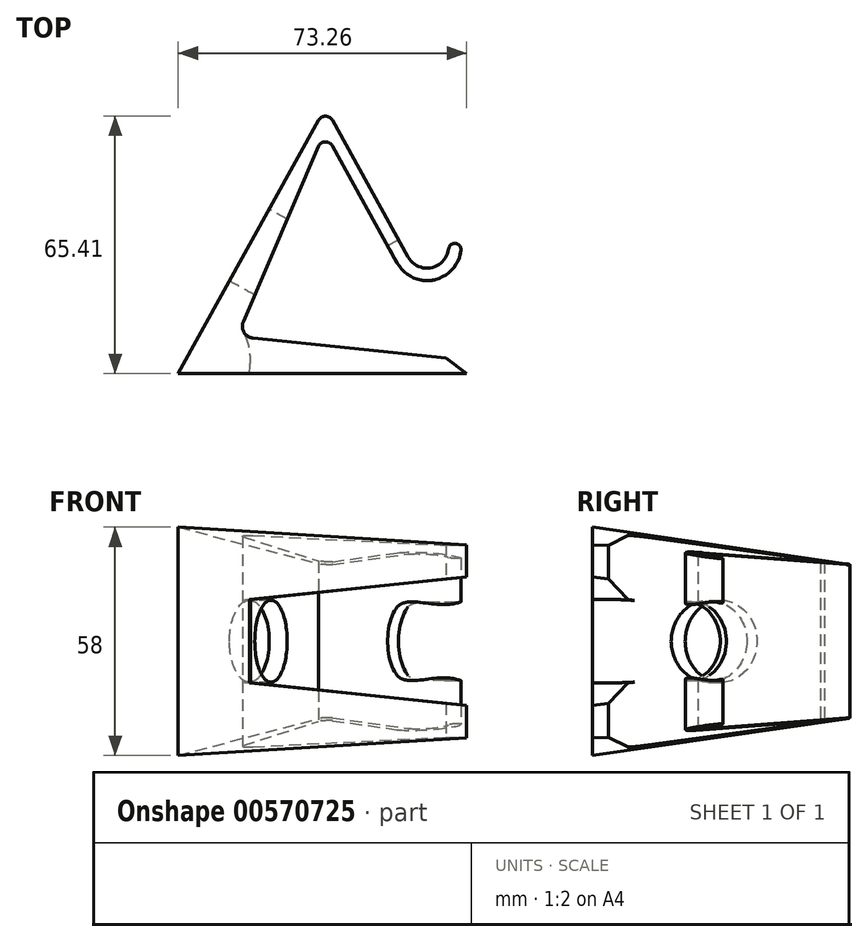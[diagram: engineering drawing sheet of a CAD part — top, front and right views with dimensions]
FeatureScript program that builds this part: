
annotation { "Feature Type Name" : "Feature", "Feature Type Description" : "" }
export const myFeature = defineFeature(function(context is Context, id is Id, definition is map)
    precondition{}
    {
        {
            var Q0;
            Q0=qCreatedBy(makeId("Top.planeOp"),FACE);
            var sketch = newSketch(context, id + "F0", { "sketchPlane" : qUnion([Q0])});
            skLineSegment(sketch, "E0", {"start": v(10.38, 11.62) * mm, "end": v(27.88, 11.62) * mm, "construction": true});
            skLineSegment(sketch, "E1", {"start": v(7.89, 47.93) * mm, "end": v(-27.76, -16.45) * mm});
            skPoint(sketch, "E2.visualSharp", {"position": v(9.6, 51.03) * mm});
            skArc(sketch, "E2.filletArc", {"start": v(11.39, 47.93) * mm, "mid": v(9.64, 48.96) * mm, "end": v(7.89, 47.93) * mm});
            skPoint(sketch, "E3.visualSharp", {"position": v(-23.5, -14.09) * mm});
            skLineSegment(sketch, "E4", {"start": v(11.39, 47.93) * mm, "end": v(30.65, 13.15) * mm});
            skLineSegment(sketch, "E5", {"start": v(-11.22, -3.27) * mm, "end": v(7.89, 41.4) * mm});
            skArc(sketch, "E6", {"start": v(11.39, 41.4) * mm, "mid": v(9.64, 42.44) * mm, "end": v(7.89, 41.4) * mm});
            skLineSegment(sketch, "E7", {"start": v(11.39, 41.4) * mm, "end": v(27.88, 11.62) * mm});
            skArc(sketch, "E8", {"start": v(30.65, 13.15) * mm, "mid": v(36.56, 10.43) * mm, "end": v(40.93, 15.25) * mm});
            skLineSegment(sketch, "E9", {"start": v(30.65, 13.15) * mm, "end": v(48.91, 23.27) * mm, "construction": true});
            skArc(sketch, "E10", {"start": v(27.88, 11.62) * mm, "mid": v(37.19, 7.33) * mm, "end": v(44.07, 14.92) * mm});
            skPoint(sketch, "E11.orphan", {"position": v(28.74, 11.62) * mm});
            skArc(sketch, "E12", {"start": v(44.07, 14.92) * mm, "mid": v(42.66, 16.66) * mm, "end": v(40.93, 15.25) * mm});
            skPoint(sketch, "E12.first.point", {"position": v(40.93, 15.25) * mm});
            skPoint(sketch, "E12.second.point", {"position": v(44.07, 14.92) * mm});
            skPoint(sketch, "E12.third.point", {"position": v(43.23, 16.49) * mm});
            skLineSegment(sketch, "E13", {"start": v(-27.76, -16.45) * mm, "end": v(45.5, -16.45) * mm});
            skLineSegment(sketch, "E14", {"start": v(-7.91, -7.53) * mm, "end": v(34.87, -11.9) * mm});
            skLineSegment(sketch, "E15", {"start": v(-7.91, -7.53) * mm, "end": v(-8.77, -7.44) * mm});
            skPoint(sketch, "E16.visualSharp", {"position": v(-12.83, -7.02) * mm});
            skArc(sketch, "E16.filletArc", {"start": v(-11.22, -3.27) * mm, "mid": v(-11.05, -5.98) * mm, "end": v(-8.77, -7.44) * mm});
            skLineSegment(sketch, "E17", {"start": v(34.87, -11.9) * mm, "end": v(40.25, -12.45) * mm});
            skLineSegment(sketch, "E18", {"start": v(40.25, -12.45) * mm, "end": v(45.5, -16.45) * mm});
            skSolve(sketch);
        }
        {
            var Q0;
            Q0=makeQuery(id+"F0.imprint","IMPRINT",FACE,{"disambiguationData":[TD([[makeQuery(id+"F0.imprint","IMPRINT",EDGE,{"derivedFrom":sQuery(id+"F0.wireOp",EDGE,"E1")}),1.0]])]});
            extrude(context, id + "F1", {"entities" : qUnion([Q0]), "depth" : 58 * mm, "offsetDistance" : 25 * mm});
        }
        {
            var Q0;
            Q0=makeQuery(id+"F1.opExtrude","SWEPT_FACE",FACE,{"disambiguationData":[OSD([sQuery(id+"F0.wireOp",EDGE,"E14"),sQuery(id+"F0.wireOp",EDGE,"E15"),sQuery(id+"F0.wireOp",EDGE,"E17")])]});
            var sketch = newSketch(context, id + "F2", { "sketchPlane" : qUnion([Q0])});
            skLineSegment(sketch, "E19", {"start": v(-41.3, 58) * mm, "end": v(7.97, 0) * mm, "construction": true});
            skLineSegment(sketch, "E20", {"start": v(-41.3, 0) * mm, "end": v(7.97, 58) * mm, "construction": true});
            skLineSegment(sketch, "E21", {"start": v(7.97, 29) * mm, "end": v(-72.88, 29) * mm, "construction": true});
            skPoint(sketch, "E21.endSnap0", {"position": v(-16.67, 29) * mm});
            skLineSegment(sketch, "E22", {"start": v(7.97, 39.64) * mm, "end": v(-83.83, 49.22) * mm});
            skLineSegment(sketch, "E23", {"start": v(7.97, 39.64) * mm, "end": v(7.97, 29) * mm});
            skLineSegment(sketch, "E24", {"start": v(-83.83, 29) * mm, "end": v(-83.83, 49.22) * mm});
            skLineSegment(sketch, "E25", {"start": v(-83.83, 29) * mm, "end": v(7.97, 29) * mm});
            skLineSegment(sketch, "E26.MirrorCS", {"start": v(7.97, 18.36) * mm, "end": v(-83.83, 8.78) * mm});
            skLineSegment(sketch, "E27.MirrorCS", {"start": v(7.97, 18.36) * mm, "end": v(7.97, 29) * mm});
            skLineSegment(sketch, "E28.MirrorCS", {"start": v(-83.83, 29) * mm, "end": v(-83.83, 8.78) * mm});
            skSolve(sketch);
        }
        {
            var Q0;
            {var subQ0=sQuery(id+"F2.wireOp",EDGE,"E28.MirrorCS");Q0=makeQuery(id+"F2.imprint","IMPRINT",FACE,{"disambiguationData":[TD([[makeQuery(id+"F2.imprint","IMPRINT",EDGE,{"derivedFrom":subQ0}),1.0]])]});}
            var Q1;
            {var subQ0=sQuery(id+"F2.wireOp",EDGE,"E24");Q1=makeQuery(id+"F2.imprint","IMPRINT",FACE,{"disambiguationData":[TD([[makeQuery(id+"F2.imprint","IMPRINT",EDGE,{"derivedFrom":subQ0}),-1.0]])]});}
            var Q2;
            {var subQ0=sQuery(id+"F2.wireOp",EDGE,"E23");Q2=makeQuery(id+"F2.imprint","IMPRINT",FACE,{"disambiguationData":[TD([[makeQuery(id+"F2.imprint","IMPRINT",EDGE,{"derivedFrom":subQ0}),-1.0]])]});}
            var Q3;
            {var subQ0=sQuery(id+"F2.wireOp",EDGE,"E27.MirrorCS");Q3=makeQuery(id+"F2.imprint","IMPRINT",FACE,{"disambiguationData":[TD([[makeQuery(id+"F2.imprint","IMPRINT",EDGE,{"derivedFrom":subQ0}),-1.0]])]});}
            extrude(context, id + "F3", {"entities" : qUnion([Q0, Q1, Q2, Q3]), "operationType" : NewBodyOperationType.REMOVE, "oppositeDirection" : true, "depth" : 25 * mm, "offsetDistance" : 25 * mm});
        }
        {
            var Q0;
            Q0=makeQuery(id+"F1.opExtrude","SWEPT_FACE",FACE,{"disambiguationData":[OSD([sQuery(id+"F0.wireOp",EDGE,"E1")])]});
            var sketch = newSketch(context, id + "F4", { "sketchPlane" : qUnion([Q0])});
            skLineSegment(sketch, "E29", {"start": v(-45.75, 0) * mm, "end": v(27.83, 58) * mm, "construction": true});
            skLineSegment(sketch, "E30", {"start": v(27.83, 0) * mm, "end": v(-45.75, 58) * mm, "construction": true});
            skLineSegment(sketch, "E31", {"start": v(-45.75, 29) * mm, "end": v(27.83, 29) * mm, "construction": true});
            skLineSegment(sketch, "E32", {"start": v(27.83, 0) * mm, "end": v(-52.66, 10.2) * mm});
            skLineSegment(sketch, "E33", {"start": v(-52.66, 10.2) * mm, "end": v(-52.66, 29) * mm});
            skLineSegment(sketch, "E34", {"start": v(-52.66, 29) * mm, "end": v(27.83, 29) * mm});
            skLineSegment(sketch, "E35", {"start": v(27.83, 0) * mm, "end": v(27.83, 1.8) * mm});
            skLineSegment(sketch, "E36", {"start": v(27.83, 1.8) * mm, "end": v(27.83, 29) * mm});
            skLineSegment(sketch, "E37.MirrorCS", {"start": v(-52.66, 47.8) * mm, "end": v(-52.66, 29) * mm});
            skLineSegment(sketch, "E38.MirrorCS", {"start": v(27.83, 58) * mm, "end": v(-52.66, 47.8) * mm});
            skLineSegment(sketch, "E39.MirrorCS", {"start": v(27.83, 56.2) * mm, "end": v(27.83, 29) * mm});
            skLineSegment(sketch, "E40.MirrorCS", {"start": v(27.83, 58) * mm, "end": v(27.83, 56.2) * mm});
            skLineSegment(sketch, "E41", {"start": v(27.83, -12.42) * mm, "end": v(-53.79, -12.42) * mm});
            skLineSegment(sketch, "E42", {"start": v(-53.79, -12.42) * mm, "end": v(-52.66, 10.2) * mm});
            skLineSegment(sketch, "E43", {"start": v(-52.66, 47.8) * mm, "end": v(-55.16, 67.52) * mm});
            skLineSegment(sketch, "E44", {"start": v(-55.16, 67.52) * mm, "end": v(27.83, 63.4) * mm});
            skLineSegment(sketch, "E45", {"start": v(27.83, 63.4) * mm, "end": v(27.83, 58) * mm});
            skLineSegment(sketch, "E46", {"start": v(27.83, -12.42) * mm, "end": v(27.83, 0) * mm});
            skSolve(sketch);
        }
        {
            var Q0;
            {var subQ1=sQuery(id+"F0.wireOp",EDGE,"E1");var subQ2=makeQuery(id+"F1.opExtrude","CAP_EDGE",EDGE,{"disambiguationData":[OSD([subQ1])],"isStart":true});Q0=makeQuery(id+"F4.imprint","IMPRINT",FACE,{"disambiguationData":[TD([[makeQuery(id+"F4.imprint","IMPRINT",EDGE,{"derivedFrom":subQ2}),1.0]])]});}
            var Q1;
            {var subQ1=sQuery(id+"F0.wireOp",EDGE,"E1");var subQ2=makeQuery(id+"F1.opExtrude","CAP_EDGE",EDGE,{"disambiguationData":[OSD([subQ1])],"isStart":false});Q1=makeQuery(id+"F4.imprint","IMPRINT",FACE,{"disambiguationData":[TD([[makeQuery(id+"F4.imprint","IMPRINT",EDGE,{"derivedFrom":subQ2}),-1.0]])]});}
            var Q2;
            Q2=makeQuery(id+"F4.imprint","IMPRINT",FACE,{"disambiguationData":[TD([[makeQuery(id+"F4.imprint","IMPRINT",EDGE,{"derivedFrom":sQuery(id+"F4.wireOp",EDGE,"E41")}),-1.0]])]});
            var Q3;
            {var subQ0=sQuery(id+"F4.wireOp",EDGE,"E43");Q3=makeQuery(id+"F4.imprint","IMPRINT",FACE,{"disambiguationData":[TD([[makeQuery(id+"F4.imprint","IMPRINT",EDGE,{"derivedFrom":subQ0}),-1.0]])]});}
            extrude(context, id + "F5", {"entities" : qUnion([Q0, Q1, Q2, Q3]), "operationType" : NewBodyOperationType.REMOVE, "oppositeDirection" : true, "depth" : 95.4 * mm, "offsetDistance" : 25 * mm});
        }
        {
            var Q0;
            Q0=makeQuery(id+"F3.boolean.opBoolean","MERGE",EDGE,{"derivedFrom":[makeQuery(id+"F1.opExtrude","SWEPT_EDGE",EDGE,{"disambiguationData":[OSD([sQuery(id+"F0.wireOp",EDGE,"E15"),sQuery(id+"F0.wireOp",EDGE,"E16.filletArc")])]}),makeQuery(id+"F3.opExtrude","CAP_EDGE",EDGE,{"disambiguationData":[OSD([sQuery(id+"F2.wireOp",EDGE,"E23"),sQuery(id+"F2.wireOp",EDGE,"E27.MirrorCS")])],"isStart":true})]});
            fillet(context, id + "F6", {"entities" : qUnion([Q0]), "radius" : 15 * mm, "tangentPropagation" : true, "allowEdgeOverflow" : false});
        }
        {
            var Q0;
            Q0=makeQuery(id+"F1.opExtrude","SWEPT_FACE",FACE,{"disambiguationData":[OSD([sQuery(id+"F0.wireOp",EDGE,"E4")])]});
            var sketch = newSketch(context, id + "F7", { "sketchPlane" : qUnion([Q0])});
            skCircle(sketch, "E47", {"center": v(-8.28, 29) * mm, "radius": 10 * mm});
            skPoint(sketch, "E47.centerSnap0", {"position": v(36.42, 29) * mm});
            skPoint(sketch, "E48", {"position": v(-3.34, 29) * mm});
            skSolve(sketch);
        }
        {
            var Q0;
            Q0 = qSketchRegion(id + "F7", true);
            extrude(context, id + "F8", {"entities" : qUnion([Q0]), "operationType" : NewBodyOperationType.REMOVE, "oppositeDirection" : true, "depth" : 10 * mm, "offsetDistance" : 25 * mm, "hasSecondDirection" : true, "secondDirectionOppositeDirection" : false, "secondDirectionDepth" : 20 * mm});
        }
        {
            var Q0;
            Q0=makeQuery(id+"F1.opExtrude","SWEPT_FACE",FACE,{"disambiguationData":[OSD([sQuery(id+"F0.wireOp",EDGE,"E1")])]});
            var sketch = newSketch(context, id + "F9", { "sketchPlane" : qUnion([Q0])});
            skCircle(sketch, "E49", {"center": v(-9.48, 29) * mm, "radius": 10.42 * mm});
            skPoint(sketch, "E49.centerSnap0", {"position": v(-45.75, 29) * mm});
            skSolve(sketch);
        }
        {
            var Q0;
            Q0 = qSketchRegion(id + "F9", true);
            extrude(context, id + "F10", {"entities" : qUnion([Q0]), "operationType" : NewBodyOperationType.REMOVE, "oppositeDirection" : true, "depth" : 25 * mm, "offsetDistance" : 25 * mm});
        }
    });
